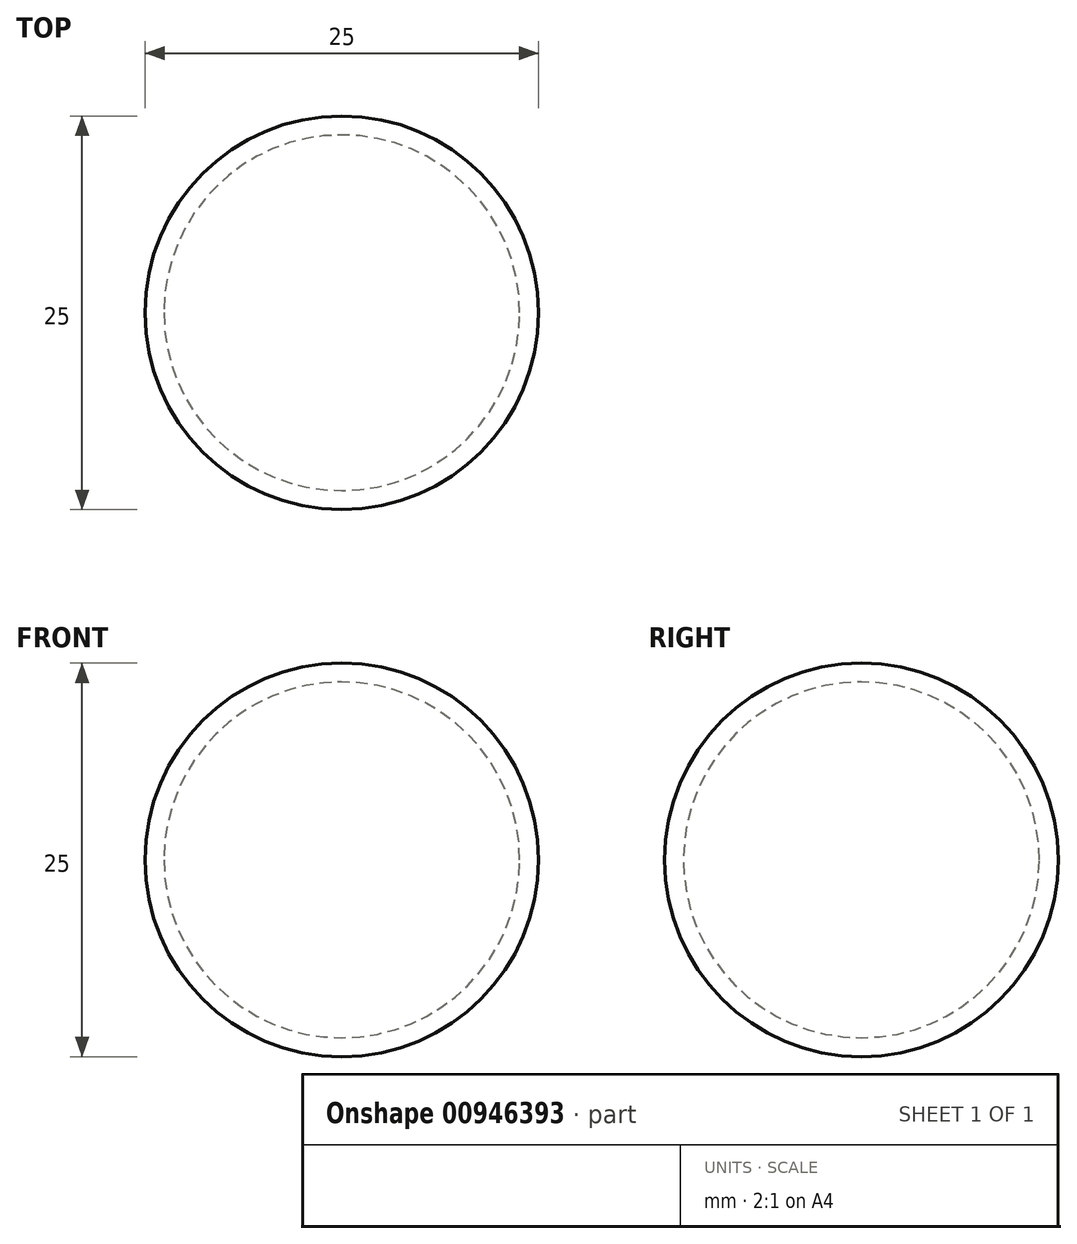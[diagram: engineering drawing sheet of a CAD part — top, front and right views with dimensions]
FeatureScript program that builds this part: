
annotation { "Feature Type Name" : "Feature", "Feature Type Description" : "" }
export const myFeature = defineFeature(function(context is Context, id is Id, definition is map)
    precondition{}
    {
        {
            var Q0;
            Q0=qCreatedBy(makeId("Top.planeOp"),FACE);
            var sketch = newSketch(context, id + "F0", { "sketchPlane" : qUnion([Q0])});
            skCircle(sketch, "E0", {"center": v(0, 0) * mm, "radius": 12.5 * mm});
            skLineSegment(sketch, "E1", {"start": v(-12.5, 0) * mm, "end": v(12.5, 0) * mm});
            skCircle(sketch, "E2.0", {"center": v(0, 0) * mm, "radius": 11.3 * mm});
            skSolve(sketch);
        }
        {
            var Q0;
            {var subQ0=sQuery(id+"F0.wireOp",EDGE,"E1");Q0=makeQuery(id+"F0.imprint","IMPRINT",FACE,{"disambiguationData":[TD([[makeQuery(id+"F0.imprint","IMPRINT",EDGE,{"derivedFrom":subQ0}),1.0]])]});}
            var Q1;
            Q1=sQuery(id+"F0.wireOp",EDGE,"E1");
            revolve(context, id + "F1", {"surfaceOperationType" : NewSurfaceOperationType.NEW, "entities" : qUnion([Q0]), "axis" : qUnion([Q1]), "revolveType" : RevolveType.FULL});
        }
    });
